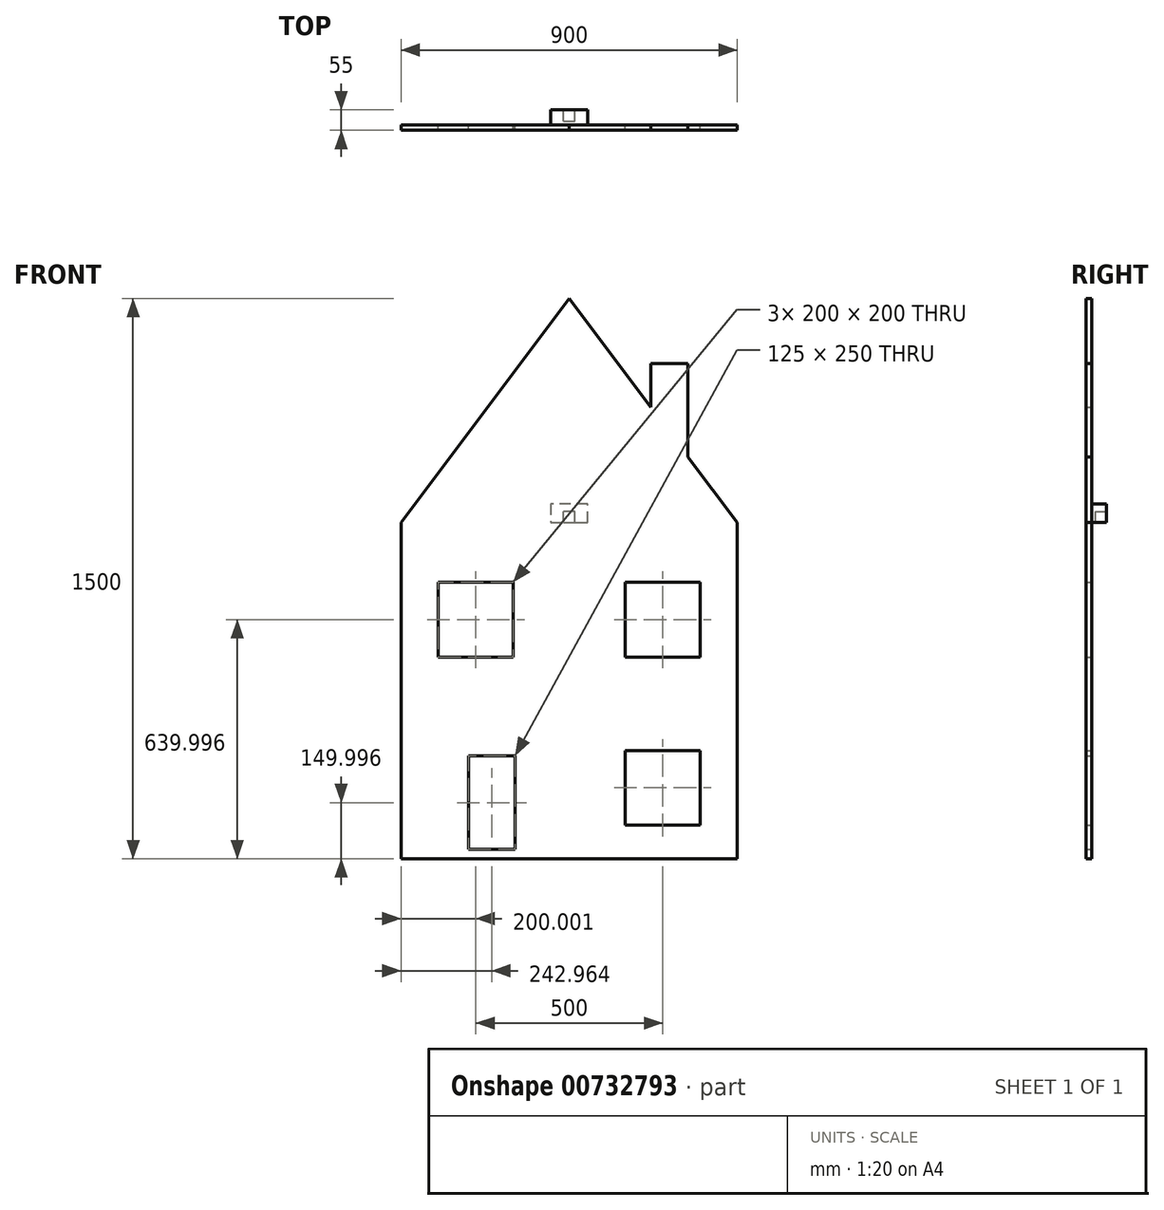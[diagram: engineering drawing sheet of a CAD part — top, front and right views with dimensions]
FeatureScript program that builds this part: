
annotation { "Feature Type Name" : "Feature", "Feature Type Description" : "" }
export const myFeature = defineFeature(function(context is Context, id is Id, definition is map)
    precondition{}
    {
        {
            var Q0;
            Q0=qCreatedBy(makeId("Front.planeOp"),FACE);
            var sketch = newSketch(context, id + "F0", { "sketchPlane" : qUnion([Q0])});
            skLineSegment(sketch, "E0.bottom", {"start": v(381.5, -608.42) * mm, "end": v(-518.5, -608.42) * mm});
            skLineSegment(sketch, "E0.top", {"start": v(381.5, 291.58) * mm, "end": v(-518.5, 291.58) * mm});
            skLineSegment(sketch, "E0.left", {"start": v(381.5, -608.42) * mm, "end": v(381.5, 291.58) * mm});
            skLineSegment(sketch, "E0.right", {"start": v(-518.5, -608.42) * mm, "end": v(-518.5, 291.58) * mm});
            skLineSegment(sketch, "E1", {"start": v(-518.5, 291.58) * mm, "end": v(-68.5, 891.58) * mm});
            skLineSegment(sketch, "E2", {"start": v(-68.5, 891.58) * mm, "end": v(381.5, 291.58) * mm});
            skLineSegment(sketch, "E3", {"start": v(-68.5, 891.58) * mm, "end": v(-68.5, -608.42) * mm, "construction": true});
            skLineSegment(sketch, "E4", {"start": v(381.5, -158.42) * mm, "end": v(-518.5, -158.42) * mm, "construction": true});
            skLineSegment(sketch, "E5", {"start": v(249.48, 467.6) * mm, "end": v(249.48, 717.6) * mm});
            skLineSegment(sketch, "E6", {"start": v(249.48, 717.6) * mm, "end": v(149.48, 717.6) * mm});
            skLineSegment(sketch, "E7", {"start": v(149.48, 717.6) * mm, "end": v(149.48, 600.92) * mm});
            skLineSegment(sketch, "E8.bottom", {"start": v(-213.05, -583.42) * mm, "end": v(-338.05, -583.42) * mm});
            skLineSegment(sketch, "E8.top", {"start": v(-213.05, -333.42) * mm, "end": v(-338.05, -333.42) * mm});
            skLineSegment(sketch, "E8.left", {"start": v(-213.05, -583.42) * mm, "end": v(-213.05, -333.42) * mm});
            skLineSegment(sketch, "E8.right", {"start": v(-338.05, -583.42) * mm, "end": v(-338.05, -333.42) * mm});
            skLineSegment(sketch, "E9.bottom", {"start": v(-418.5, 131.58) * mm, "end": v(-218.5, 131.58) * mm});
            skLineSegment(sketch, "E9.top", {"start": v(-418.5, -68.42) * mm, "end": v(-218.5, -68.42) * mm});
            skLineSegment(sketch, "E9.left", {"start": v(-418.5, 131.58) * mm, "end": v(-418.5, -68.42) * mm});
            skLineSegment(sketch, "E9.right", {"start": v(-218.5, 131.58) * mm, "end": v(-218.5, -68.42) * mm});
            skLineSegment(sketch, "E10.bottom", {"start": v(281.5, -68.42) * mm, "end": v(81.5, -68.42) * mm});
            skLineSegment(sketch, "E10.top", {"start": v(281.5, 131.58) * mm, "end": v(81.5, 131.58) * mm});
            skLineSegment(sketch, "E10.left", {"start": v(281.5, -68.42) * mm, "end": v(281.5, 131.58) * mm});
            skLineSegment(sketch, "E10.right", {"start": v(81.5, -68.42) * mm, "end": v(81.5, 131.58) * mm});
            skLineSegment(sketch, "E11.bottom", {"start": v(281.5, -518.42) * mm, "end": v(81.5, -518.42) * mm});
            skLineSegment(sketch, "E11.top", {"start": v(281.5, -318.42) * mm, "end": v(81.5, -318.42) * mm});
            skLineSegment(sketch, "E11.left", {"start": v(281.5, -518.42) * mm, "end": v(281.5, -318.42) * mm});
            skLineSegment(sketch, "E11.right", {"start": v(81.5, -518.42) * mm, "end": v(81.5, -318.42) * mm});
            skSolve(sketch);
        }
        {
            var Q0;
            Q0 = qSketchRegion(id + "F0", true);
            extrude(context, id + "F1", {"entities" : qUnion([Q0]), "depth" : 15 * mm, "offsetDistance" : 25 * mm});
        }
        {
            var Q0;
            Q0=makeQuery(id+"F1.opExtrude","CAP_FACE",FACE,{"disambiguationData":[OSD([sQuery(id+"F0.wireOp",EDGE,"E0.bottom"),sQuery(id+"F0.wireOp",EDGE,"E0.left"),sQuery(id+"F0.wireOp",EDGE,"E0.right"),sQuery(id+"F0.wireOp",EDGE,"E1"),sQuery(id+"F0.wireOp",EDGE,"E2"),sQuery(id+"F0.wireOp",EDGE,"E5"),sQuery(id+"F0.wireOp",EDGE,"E6"),sQuery(id+"F0.wireOp",EDGE,"E7"),sQuery(id+"F0.wireOp",EDGE,"E8.bottom"),sQuery(id+"F0.wireOp",EDGE,"E8.top"),sQuery(id+"F0.wireOp",EDGE,"E8.left"),sQuery(id+"F0.wireOp",EDGE,"E8.right"),sQuery(id+"F0.wireOp",EDGE,"E9.bottom"),sQuery(id+"F0.wireOp",EDGE,"E9.top"),sQuery(id+"F0.wireOp",EDGE,"E9.left"),sQuery(id+"F0.wireOp",EDGE,"E9.right"),sQuery(id+"F0.wireOp",EDGE,"E10.bottom"),sQuery(id+"F0.wireOp",EDGE,"E10.top"),sQuery(id+"F0.wireOp",EDGE,"E10.left"),sQuery(id+"F0.wireOp",EDGE,"E10.right"),sQuery(id+"F0.wireOp",EDGE,"E11.bottom"),sQuery(id+"F0.wireOp",EDGE,"E11.top"),sQuery(id+"F0.wireOp",EDGE,"E11.left"),sQuery(id+"F0.wireOp",EDGE,"E11.right")])],"isStart":true});
            var sketch = newSketch(context, id + "F2", { "sketchPlane" : qUnion([Q0])});
            skLineSegment(sketch, "E12", {"start": v(-381.5, 291.58) * mm, "end": v(518.5, 291.58) * mm, "construction": true});
            skLineSegment(sketch, "E13", {"start": v(68.5, 291.58) * mm, "end": v(18.5, 291.58) * mm});
            skLineSegment(sketch, "E14", {"start": v(18.5, 291.58) * mm, "end": v(18.5, 341.58) * mm});
            skLineSegment(sketch, "E15", {"start": v(18.5, 341.58) * mm, "end": v(118.5, 341.58) * mm});
            skLineSegment(sketch, "E16", {"start": v(118.5, 341.58) * mm, "end": v(118.5, 291.58) * mm});
            skLineSegment(sketch, "E17", {"start": v(118.5, 291.58) * mm, "end": v(68.5, 291.58) * mm});
            skSolve(sketch);
        }
        {
            var Q0;
            Q0 = qSketchRegion(id + "F2", true);
            extrude(context, id + "F3", {"entities" : qUnion([Q0]), "operationType" : NewBodyOperationType.ADD, "depth" : 40 * mm, "offsetDistance" : 25 * mm});
        }
        {
            var Q0;
            Q0=makeQuery(id+"F3.opExtrude","CAP_FACE",FACE,{"disambiguationData":[OSD([sQuery(id+"F2.wireOp",EDGE,"E13"),sQuery(id+"F2.wireOp",EDGE,"E14"),sQuery(id+"F2.wireOp",EDGE,"E15"),sQuery(id+"F2.wireOp",EDGE,"E16"),sQuery(id+"F2.wireOp",EDGE,"E17")])],"isStart":false});
            var sketch = newSketch(context, id + "F4", { "sketchPlane" : qUnion([Q0])});
            skLineSegment(sketch, "E18.bottom", {"start": v(53.5, 291.58) * mm, "end": v(83.5, 291.58) * mm});
            skLineSegment(sketch, "E18.top", {"start": v(53.5, 321.58) * mm, "end": v(83.5, 321.58) * mm});
            skLineSegment(sketch, "E18.left", {"start": v(53.5, 291.58) * mm, "end": v(53.5, 321.58) * mm});
            skLineSegment(sketch, "E18.right", {"start": v(83.5, 291.58) * mm, "end": v(83.5, 321.58) * mm});
            skSolve(sketch);
        }
        {
            var Q0;
            Q0 = qSketchRegion(id + "F4", true);
            extrude(context, id + "F5", {"entities" : qUnion([Q0]), "operationType" : NewBodyOperationType.REMOVE, "oppositeDirection" : true, "depth" : 30 * mm, "offsetDistance" : 25 * mm});
        }
    });
